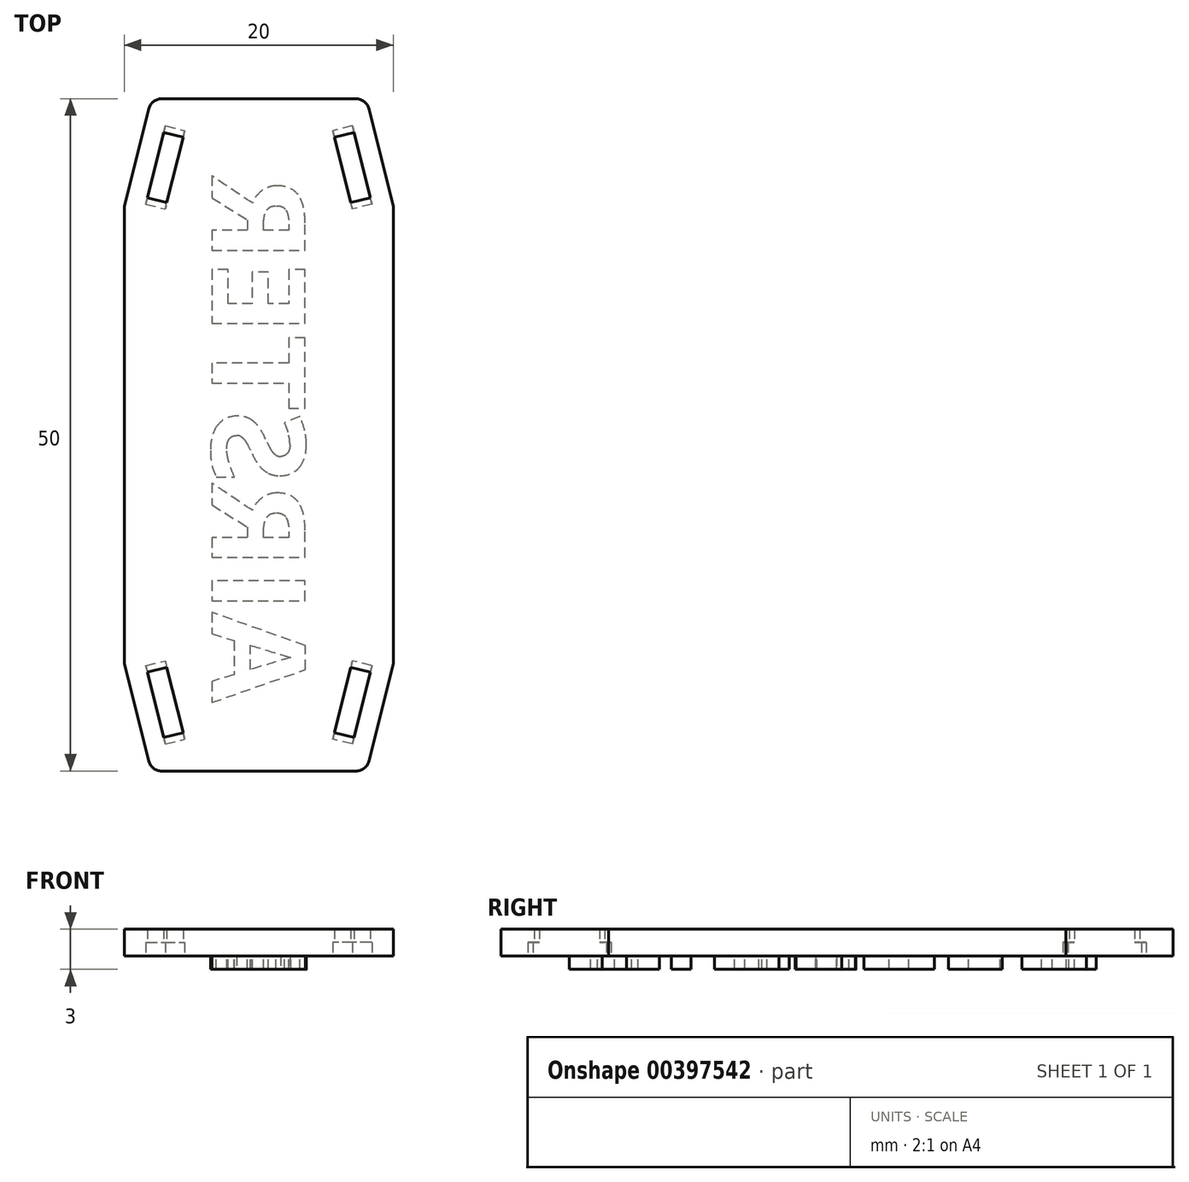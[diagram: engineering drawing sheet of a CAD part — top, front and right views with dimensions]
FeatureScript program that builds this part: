
annotation { "Feature Type Name" : "Feature", "Feature Type Description" : "" }
export const myFeature = defineFeature(function(context is Context, id is Id, definition is map)
    precondition{}
    {
        {
            var Q0;
            Q0=qCreatedBy(makeId("Top.planeOp"),FACE);
            var sketch = newSketch(context, id + "F0", { "sketchPlane" : qUnion([Q0])});
            skLineSegment(sketch, "E0.bottom", {"start": v(10, -25) * mm, "end": v(-10, -25) * mm});
            skLineSegment(sketch, "E0.top", {"start": v(10, 25) * mm, "end": v(-10, 25) * mm});
            skLineSegment(sketch, "E0.left", {"start": v(10, -25) * mm, "end": v(10, 25) * mm});
            skLineSegment(sketch, "E0.right", {"start": v(-10, -25) * mm, "end": v(-10, 25) * mm});
            skSolve(sketch);
        }
        {
            var Q0;
            Q0=qSketchRegion(id+"F0",true);
            var Q1;
            {var subQ1=sQuery(id+"F0.wireOp",EDGE,"18e5cb70-7c8f-420a-958b-2ec66c54b7be.1.3");var subQ3=sQuery(id+"F0.wireOp",EDGE,"18e5cb70-7c8f-420a-958b-2ec66c54b7be.2.2");var subQ4=makeQuery(id+"F0.imprint","INTERSECT",VERTEX,{"derivedFrom":[subQ1,subQ3]});Q1=makeQuery(id+"F0.imprint","IMPRINT",FACE,{"disambiguationData":[TD([[makeQuery(id+"F0.imprint","IMPRINT",EDGE,{"disambiguationData":[TD([[subQ4,-1.0]])],"derivedFrom":subQ1}),1.0]])]});}
            var Q2;
            {var subQ1=sQuery(id+"F0.wireOp",EDGE,"df0GztRu-gwq4-BQam-XN3u-W2BSvXK0RSs7.top");var subQ3=sQuery(id+"F0.wireOp",EDGE,"18e5cb70-7c8f-420a-958b-2ec66c54b7be.1.2");var subQ4=makeQuery(id+"F0.imprint","INTERSECT",VERTEX,{"derivedFrom":[subQ1,subQ3]});Q2=makeQuery(id+"F0.imprint","IMPRINT",FACE,{"disambiguationData":[TD([[makeQuery(id+"F0.imprint","IMPRINT",EDGE,{"disambiguationData":[TD([[subQ4,-1.0]])],"derivedFrom":subQ1}),1.0]])]});}
            var Q3;
            {var subQ1=sQuery(id+"F0.wireOp",EDGE,"df0GztRu-gwq4-BQam-XN3u-W2BSvXK0RSs7.bottom");var subQ3=sQuery(id+"F0.wireOp",EDGE,"bce8df73-cd66-45c5-b75a-186190c6299e.6.3.0");var subQ4=makeQuery(id+"F0.imprint","INTERSECT",VERTEX,{"derivedFrom":[subQ1,subQ3]});Q3=makeQuery(id+"F0.imprint","IMPRINT",FACE,{"disambiguationData":[TD([[makeQuery(id+"F0.imprint","IMPRINT",EDGE,{"disambiguationData":[TD([[subQ4,-1.0]])],"derivedFrom":subQ1}),-1.0]])]});}
            var Q4;
            {var subQ1=sQuery(id+"F0.wireOp",EDGE,"18e5cb70-7c8f-420a-958b-2ec66c54b7be.2.3");var subQ3=sQuery(id+"F0.wireOp",EDGE,"bce8df73-cd66-45c5-b75a-186190c6299e.3.3.0");var subQ4=makeQuery(id+"F0.imprint","INTERSECT",VERTEX,{"derivedFrom":[subQ1,subQ3]});Q4=makeQuery(id+"F0.imprint","IMPRINT",FACE,{"disambiguationData":[TD([[makeQuery(id+"F0.imprint","IMPRINT",EDGE,{"disambiguationData":[TD([[subQ4,-1.0]])],"derivedFrom":subQ1}),1.0]])]});}
            extrude(context, id + "F1", {"entities" : qUnion([Q0, Q1, Q2, Q3, Q4]), "oppositeDirection" : true, "depth" : 2 * mm});
        }
        {
            var Q0;
            Q0=makeQuery(id+"F1.opExtrude","SWEPT_EDGE",EDGE,{"disambiguationData":[OSD([sQuery(id+"F0.wireOp",EDGE,"E0.top"),sQuery(id+"F0.wireOp",EDGE,"E0.right")])]});
            var Q1;
            Q1=makeQuery(id+"F1.opExtrude","SWEPT_EDGE",EDGE,{"disambiguationData":[OSD([sQuery(id+"F0.wireOp",EDGE,"E0.top"),sQuery(id+"F0.wireOp",EDGE,"E0.left")])]});
            chamfer(context, id + "F2", {"entities" : qUnion([Q0, Q1]), "chamferType" : ChamferType.TWO_OFFSETS, "width1" : 8 * mm, "oppositeDirection" : true, "width2" : 2 * mm, "tangentPropagation" : true});
        }
        {
            var Q0;
            Q0=makeQuery(id+"F1.opExtrude","SWEPT_EDGE",EDGE,{"disambiguationData":[OSD([sQuery(id+"F0.wireOp",EDGE,"E0.bottom"),sQuery(id+"F0.wireOp",EDGE,"E0.right")])]});
            var Q1;
            Q1=makeQuery(id+"F1.opExtrude","SWEPT_EDGE",EDGE,{"disambiguationData":[OSD([sQuery(id+"F0.wireOp",EDGE,"E0.bottom"),sQuery(id+"F0.wireOp",EDGE,"E0.left")])]});
            chamfer(context, id + "F3", {"entities" : qUnion([Q0, Q1]), "chamferType" : ChamferType.TWO_OFFSETS, "width1" : 2 * mm, "oppositeDirection" : true, "width2" : 8 * mm, "tangentPropagation" : true});
        }
        {
            var Q0;
            {var subQ0=sQuery(id+"F0.wireOp",EDGE,"E0.bottom");Q0=makeQuery(id+"F3.opChamfer","BLEND_EDGE",EDGE,{"blendedFrom":[makeQuery(id+"F1.opExtrude","SWEPT_EDGE",EDGE,{"disambiguationData":[OSD([subQ0,sQuery(id+"F0.wireOp",EDGE,"E0.left")])]}),makeQuery(id+"F1.opExtrude","SWEPT_FACE",FACE,{"disambiguationData":[OSD([subQ0])]})],"blendedInto":[makeQuery(id+"F1.opExtrude","SWEPT_FACE",FACE,{"disambiguationData":[OSD([subQ0])]})]});}
            var Q1;
            {var subQ0=sQuery(id+"F0.wireOp",EDGE,"E0.bottom");Q1=makeQuery(id+"F3.opChamfer","BLEND_EDGE",EDGE,{"blendedFrom":[makeQuery(id+"F1.opExtrude","SWEPT_EDGE",EDGE,{"disambiguationData":[OSD([subQ0,sQuery(id+"F0.wireOp",EDGE,"E0.right")])]}),makeQuery(id+"F1.opExtrude","SWEPT_FACE",FACE,{"disambiguationData":[OSD([subQ0])]})],"blendedInto":[makeQuery(id+"F1.opExtrude","SWEPT_FACE",FACE,{"disambiguationData":[OSD([subQ0])]})]});}
            var Q2;
            {var subQ0=sQuery(id+"F0.wireOp",EDGE,"E0.top");Q2=makeQuery(id+"F2.opChamfer","BLEND_EDGE",EDGE,{"blendedFrom":[makeQuery(id+"F1.opExtrude","SWEPT_EDGE",EDGE,{"disambiguationData":[OSD([subQ0,sQuery(id+"F0.wireOp",EDGE,"E0.right")])]}),makeQuery(id+"F1.opExtrude","SWEPT_FACE",FACE,{"disambiguationData":[OSD([subQ0])]})],"blendedInto":[makeQuery(id+"F1.opExtrude","SWEPT_FACE",FACE,{"disambiguationData":[OSD([subQ0])]})]});}
            var Q3;
            {var subQ0=sQuery(id+"F0.wireOp",EDGE,"E0.top");Q3=makeQuery(id+"F2.opChamfer","BLEND_EDGE",EDGE,{"blendedFrom":[makeQuery(id+"F1.opExtrude","SWEPT_EDGE",EDGE,{"disambiguationData":[OSD([subQ0,sQuery(id+"F0.wireOp",EDGE,"E0.left")])]}),makeQuery(id+"F1.opExtrude","SWEPT_FACE",FACE,{"disambiguationData":[OSD([subQ0])]})],"blendedInto":[makeQuery(id+"F1.opExtrude","SWEPT_FACE",FACE,{"disambiguationData":[OSD([subQ0])]})]});}
            fillet(context, id + "F4", {"entities" : qUnion([Q0, Q1, Q2, Q3]), "radius" : 1 * mm, "tangentPropagation" : true, "allowEdgeOverflow" : false});
        }
        {
            var Q0;
            Q0=makeQuery(id+"F1.opExtrude","CAP_FACE",FACE,{"disambiguationData":[OSD([sQuery(id+"F0.wireOp",EDGE,"E0.bottom"),sQuery(id+"F0.wireOp",EDGE,"E0.top"),sQuery(id+"F0.wireOp",EDGE,"E0.left"),sQuery(id+"F0.wireOp",EDGE,"E0.right"),sQuery(id+"F0.wireOp",EDGE,"df0GztRu-gwq4-BQam-XN3u-W2BSvXK0RSs7.bottom"),sQuery(id+"F0.wireOp",EDGE,"df0GztRu-gwq4-BQam-XN3u-W2BSvXK0RSs7.top"),sQuery(id+"F0.wireOp",EDGE,"QBaO1Gub-vl3L-KiVP-tVlY-TxEHB5Py9miZ"),sQuery(id+"F0.wireOp",EDGE,"18e5cb70-7c8f-420a-958b-2ec66c54b7be.1.1"),sQuery(id+"F0.wireOp",EDGE,"18e5cb70-7c8f-420a-958b-2ec66c54b7be.1.2"),sQuery(id+"F0.wireOp",EDGE,"18e5cb70-7c8f-420a-958b-2ec66c54b7be.1.3"),sQuery(id+"F0.wireOp",EDGE,"18e5cb70-7c8f-420a-958b-2ec66c54b7be.2.1"),sQuery(id+"F0.wireOp",EDGE,"18e5cb70-7c8f-420a-958b-2ec66c54b7be.2.2"),sQuery(id+"F0.wireOp",EDGE,"18e5cb70-7c8f-420a-958b-2ec66c54b7be.2.3"),sQuery(id+"F0.wireOp",EDGE,"bce8df73-cd66-45c5-b75a-186190c6299e.1.3.0"),sQuery(id+"F0.wireOp",EDGE,"bce8df73-cd66-45c5-b75a-186190c6299e.3.3.0"),sQuery(id+"F0.wireOp",EDGE,"bce8df73-cd66-45c5-b75a-186190c6299e.6.3.0")])],"isStart":false});
            var sketch = newSketch(context, id + "F5", { "sketchPlane" : qUnion([Q0])});
            skLineSegment(sketch, "E1.bottom", {"start": v(-7.08, 22.5) * mm, "end": v(-5.62, 22.14) * mm});
            skLineSegment(sketch, "E1.top", {"start": v(-8.3, 17.65) * mm, "end": v(-6.84, 17.29) * mm});
            skLineSegment(sketch, "E1.left", {"start": v(-7.08, 22.5) * mm, "end": v(-8.3, 17.65) * mm});
            skLineSegment(sketch, "E1.right", {"start": v(-5.62, 22.14) * mm, "end": v(-6.84, 17.29) * mm});
            skLineSegment(sketch, "E2", {"start": v(0, 25) * mm, "end": v(0, -25) * mm, "construction": true});
            skLineSegment(sketch, "E3", {"start": v(-10, 0) * mm, "end": v(10, 0) * mm, "construction": true});
            skText(sketch, "E4", { "text": "AIRSTER", "fontName": "OpenSans-Bold.ttf"});
            skPoint(sketch, "E5", {"position": v(0, 19.91) * mm});
            skLineSegment(sketch, "E6.0", {"start": v(-6.96, 22.99) * mm, "end": v(-5.5, 22.62) * mm});
            skLineSegment(sketch, "E7", {"start": v(-7.08, 22.5) * mm, "end": v(-6.96, 22.99) * mm});
            skLineSegment(sketch, "E8", {"start": v(-5.62, 22.14) * mm, "end": v(-5.5, 22.62) * mm});
            skLineSegment(sketch, "E9.0", {"start": v(-8.41, 17.16) * mm, "end": v(-6.96, 16.8) * mm});
            skLineSegment(sketch, "E10", {"start": v(-6.96, 16.8) * mm, "end": v(-6.84, 17.29) * mm});
            skLineSegment(sketch, "E11", {"start": v(-8.41, 17.16) * mm, "end": v(-8.3, 17.65) * mm});
            skLineSegment(sketch, "E12.MirrorCS", {"start": v(-5.62, -22.14) * mm, "end": v(-5.5, -22.62) * mm});
            skLineSegment(sketch, "E13.MirrorCS", {"start": v(-6.96, -16.8) * mm, "end": v(-6.84, -17.29) * mm});
            skLineSegment(sketch, "E14.MirrorCS", {"start": v(-7.08, -22.5) * mm, "end": v(-6.96, -22.99) * mm});
            skLineSegment(sketch, "E15.MirrorCS", {"start": v(-8.41, -17.16) * mm, "end": v(-8.3, -17.65) * mm});
            skLineSegment(sketch, "E16.MirrorCS", {"start": v(-7.08, -22.5) * mm, "end": v(-5.62, -22.14) * mm});
            skLineSegment(sketch, "E17.MirrorCS", {"start": v(-8.3, -17.65) * mm, "end": v(-6.84, -17.29) * mm});
            skLineSegment(sketch, "E18.MirrorCS", {"start": v(-8.41, -17.16) * mm, "end": v(-6.96, -16.8) * mm});
            skLineSegment(sketch, "E19.MirrorCS", {"start": v(-6.96, -22.99) * mm, "end": v(-5.5, -22.62) * mm});
            skLineSegment(sketch, "E20.MirrorCS", {"start": v(-5.62, -22.14) * mm, "end": v(-6.84, -17.29) * mm});
            skLineSegment(sketch, "E21.MirrorCS", {"start": v(-7.08, -22.5) * mm, "end": v(-8.3, -17.65) * mm});
            skLineSegment(sketch, "E22.MirrorCS", {"start": v(5.62, -22.14) * mm, "end": v(5.5, -22.62) * mm});
            skLineSegment(sketch, "E23.MirrorCS", {"start": v(7.08, -22.5) * mm, "end": v(6.96, -22.99) * mm});
            skLineSegment(sketch, "E24.MirrorCS", {"start": v(8.41, -17.16) * mm, "end": v(8.3, -17.65) * mm});
            skLineSegment(sketch, "E25.MirrorCS", {"start": v(6.96, -16.8) * mm, "end": v(6.84, -17.29) * mm});
            skLineSegment(sketch, "E26.MirrorCS", {"start": v(5.62, -22.14) * mm, "end": v(6.84, -17.29) * mm});
            skLineSegment(sketch, "E27.MirrorCS", {"start": v(8.3, -17.65) * mm, "end": v(6.84, -17.29) * mm});
            skLineSegment(sketch, "E28.MirrorCS", {"start": v(7.08, -22.5) * mm, "end": v(8.3, -17.65) * mm});
            skLineSegment(sketch, "E29.MirrorCS", {"start": v(7.08, -22.5) * mm, "end": v(5.62, -22.14) * mm});
            skLineSegment(sketch, "E30.MirrorCS", {"start": v(8.41, -17.16) * mm, "end": v(6.96, -16.8) * mm});
            skLineSegment(sketch, "E31.MirrorCS", {"start": v(6.96, -22.99) * mm, "end": v(5.5, -22.62) * mm});
            skLineSegment(sketch, "E32.MirrorCS", {"start": v(7.08, 22.5) * mm, "end": v(6.96, 22.99) * mm});
            skLineSegment(sketch, "E33.MirrorCS", {"start": v(5.62, 22.14) * mm, "end": v(5.5, 22.62) * mm});
            skLineSegment(sketch, "E34.MirrorCS", {"start": v(6.96, 16.8) * mm, "end": v(6.84, 17.29) * mm});
            skLineSegment(sketch, "E35.MirrorCS", {"start": v(8.41, 17.16) * mm, "end": v(8.3, 17.65) * mm});
            skLineSegment(sketch, "E36.MirrorCS", {"start": v(6.96, 22.99) * mm, "end": v(5.5, 22.62) * mm});
            skLineSegment(sketch, "E37.MirrorCS", {"start": v(8.3, 17.65) * mm, "end": v(6.84, 17.29) * mm});
            skLineSegment(sketch, "E38.MirrorCS", {"start": v(8.41, 17.16) * mm, "end": v(6.96, 16.8) * mm});
            skLineSegment(sketch, "E39.MirrorCS", {"start": v(7.08, 22.5) * mm, "end": v(5.62, 22.14) * mm});
            skLineSegment(sketch, "E40.MirrorCS", {"start": v(5.62, 22.14) * mm, "end": v(6.84, 17.29) * mm});
            skLineSegment(sketch, "E41.MirrorCS", {"start": v(7.08, 22.5) * mm, "end": v(8.3, 17.65) * mm});
            const initialGuessF5  = {"E4": [-0.0035, 0.01991, 0, -1, 0.007]};
            skSetInitialGuess(sketch, initialGuessF5);
            skSolve(sketch);
        }
        {
            var Q0;
            Q0=makeQuery(id+"F5.imprint","IMPRINT",FACE,{"disambiguationData":[TD([[makeQuery(id+"F5.imprint","IMPRINT",EDGE,{"derivedFrom":sQuery(id+"F5.wireOp",EDGE,"E1.bottom")}),-1.0]])]});
            var Q1;
            Q1=makeQuery(id+"F5.imprint","IMPRINT",FACE,{"disambiguationData":[TD([[makeQuery(id+"F5.imprint","IMPRINT",EDGE,{"derivedFrom":sQuery(id+"F5.wireOp",EDGE,"E37.MirrorCS")}),-1.0]])]});
            var Q2;
            Q2=makeQuery(id+"F5.imprint","IMPRINT",FACE,{"disambiguationData":[TD([[makeQuery(id+"F5.imprint","IMPRINT",EDGE,{"derivedFrom":sQuery(id+"F5.wireOp",EDGE,"E26.MirrorCS")}),-1.0]])]});
            var Q3;
            Q3=makeQuery(id+"F5.imprint","IMPRINT",FACE,{"disambiguationData":[TD([[makeQuery(id+"F5.imprint","IMPRINT",EDGE,{"derivedFrom":sQuery(id+"F5.wireOp",EDGE,"E16.MirrorCS")}),1.0]])]});
            extrude(context, id + "F6", {"entities" : qUnion([Q0, Q1, Q2, Q3]), "operationType" : NewBodyOperationType.REMOVE, "endBound" : BoundingType.THROUGH_ALL, "oppositeDirection" : true, "depth" : 25 * mm});
        }
        {
            var Q0;
            Q0=makeQuery(id+"F5.imprint","IMPRINT",FACE,{"disambiguationData":[TD([[makeQuery(id+"F5.imprint","IMPRINT",EDGE,{"derivedFrom":sQuery(id+"F5.wireOp",EDGE,"E4.sketch_text.stroke-0")}),-1.0]])]});
            var Q1;
            Q1=makeQuery(id+"F5.imprint","IMPRINT",FACE,{"disambiguationData":[TD([[makeQuery(id+"F5.imprint","IMPRINT",EDGE,{"derivedFrom":sQuery(id+"F5.wireOp",EDGE,"E4.sketch_text.stroke-12")}),-1.0]])]});
            var Q2;
            Q2=makeQuery(id+"F5.imprint","IMPRINT",FACE,{"disambiguationData":[TD([[makeQuery(id+"F5.imprint","IMPRINT",EDGE,{"derivedFrom":sQuery(id+"F5.wireOp",EDGE,"E4.sketch_text.stroke-16")}),-1.0]])]});
            var Q3;
            Q3=makeQuery(id+"F5.imprint","IMPRINT",FACE,{"disambiguationData":[TD([[makeQuery(id+"F5.imprint","IMPRINT",EDGE,{"derivedFrom":sQuery(id+"F5.wireOp",EDGE,"E4.sketch_text.stroke-35")}),-1.0]])]});
            var Q4;
            Q4=makeQuery(id+"F5.imprint","IMPRINT",FACE,{"disambiguationData":[TD([[makeQuery(id+"F5.imprint","IMPRINT",EDGE,{"derivedFrom":sQuery(id+"F5.wireOp",EDGE,"E4.sketch_text.stroke-63")}),-1.0]])]});
            var Q5;
            Q5=makeQuery(id+"F5.imprint","IMPRINT",FACE,{"disambiguationData":[TD([[makeQuery(id+"F5.imprint","IMPRINT",EDGE,{"derivedFrom":sQuery(id+"F5.wireOp",EDGE,"E4.sketch_text.stroke-71")}),-1.0]])]});
            var Q6;
            Q6=makeQuery(id+"F5.imprint","IMPRINT",FACE,{"disambiguationData":[TD([[makeQuery(id+"F5.imprint","IMPRINT",EDGE,{"derivedFrom":sQuery(id+"F5.wireOp",EDGE,"E4.sketch_text.stroke-83")}),-1.0]])]});
            extrude(context, id + "F7", {"entities" : qUnion([Q0, Q1, Q2, Q3, Q4, Q5, Q6]), "operationType" : NewBodyOperationType.ADD, "depth" : 1 * mm});
        }
        {
            var Q0;
            Q0=makeQuery(id+"F5.imprint","IMPRINT",FACE,{"disambiguationData":[TD([[makeQuery(id+"F5.imprint","IMPRINT",EDGE,{"derivedFrom":sQuery(id+"F5.wireOp",EDGE,"E32.MirrorCS")}),1.0]])]});
            var Q1;
            Q1=makeQuery(id+"F5.imprint","IMPRINT",FACE,{"disambiguationData":[TD([[makeQuery(id+"F5.imprint","IMPRINT",EDGE,{"derivedFrom":sQuery(id+"F5.wireOp",EDGE,"E34.MirrorCS")}),-1.0]])]});
            var Q2;
            Q2=makeQuery(id+"F5.imprint","IMPRINT",FACE,{"disambiguationData":[TD([[makeQuery(id+"F5.imprint","IMPRINT",EDGE,{"derivedFrom":sQuery(id+"F5.wireOp",EDGE,"E1.bottom")}),1.0]])]});
            var Q3;
            Q3=makeQuery(id+"F5.imprint","IMPRINT",FACE,{"disambiguationData":[TD([[makeQuery(id+"F5.imprint","IMPRINT",EDGE,{"derivedFrom":sQuery(id+"F5.wireOp",EDGE,"E1.top")}),-1.0]])]});
            var Q4;
            Q4=makeQuery(id+"F5.imprint","IMPRINT",FACE,{"disambiguationData":[TD([[makeQuery(id+"F5.imprint","IMPRINT",EDGE,{"derivedFrom":sQuery(id+"F5.wireOp",EDGE,"E24.MirrorCS")}),-1.0]])]});
            var Q5;
            Q5=makeQuery(id+"F5.imprint","IMPRINT",FACE,{"disambiguationData":[TD([[makeQuery(id+"F5.imprint","IMPRINT",EDGE,{"derivedFrom":sQuery(id+"F5.wireOp",EDGE,"E22.MirrorCS")}),1.0]])]});
            var Q6;
            Q6=makeQuery(id+"F5.imprint","IMPRINT",FACE,{"disambiguationData":[TD([[makeQuery(id+"F5.imprint","IMPRINT",EDGE,{"derivedFrom":sQuery(id+"F5.wireOp",EDGE,"E12.MirrorCS")}),-1.0]])]});
            var Q7;
            Q7=makeQuery(id+"F5.imprint","IMPRINT",FACE,{"disambiguationData":[TD([[makeQuery(id+"F5.imprint","IMPRINT",EDGE,{"derivedFrom":sQuery(id+"F5.wireOp",EDGE,"E13.MirrorCS")}),-1.0]])]});
            extrude(context, id + "F8", {"entities" : qUnion([Q0, Q1, Q2, Q3, Q4, Q5, Q6, Q7]), "operationType" : NewBodyOperationType.REMOVE, "oppositeDirection" : true, "depth" : 1 * mm});
        }
    });
